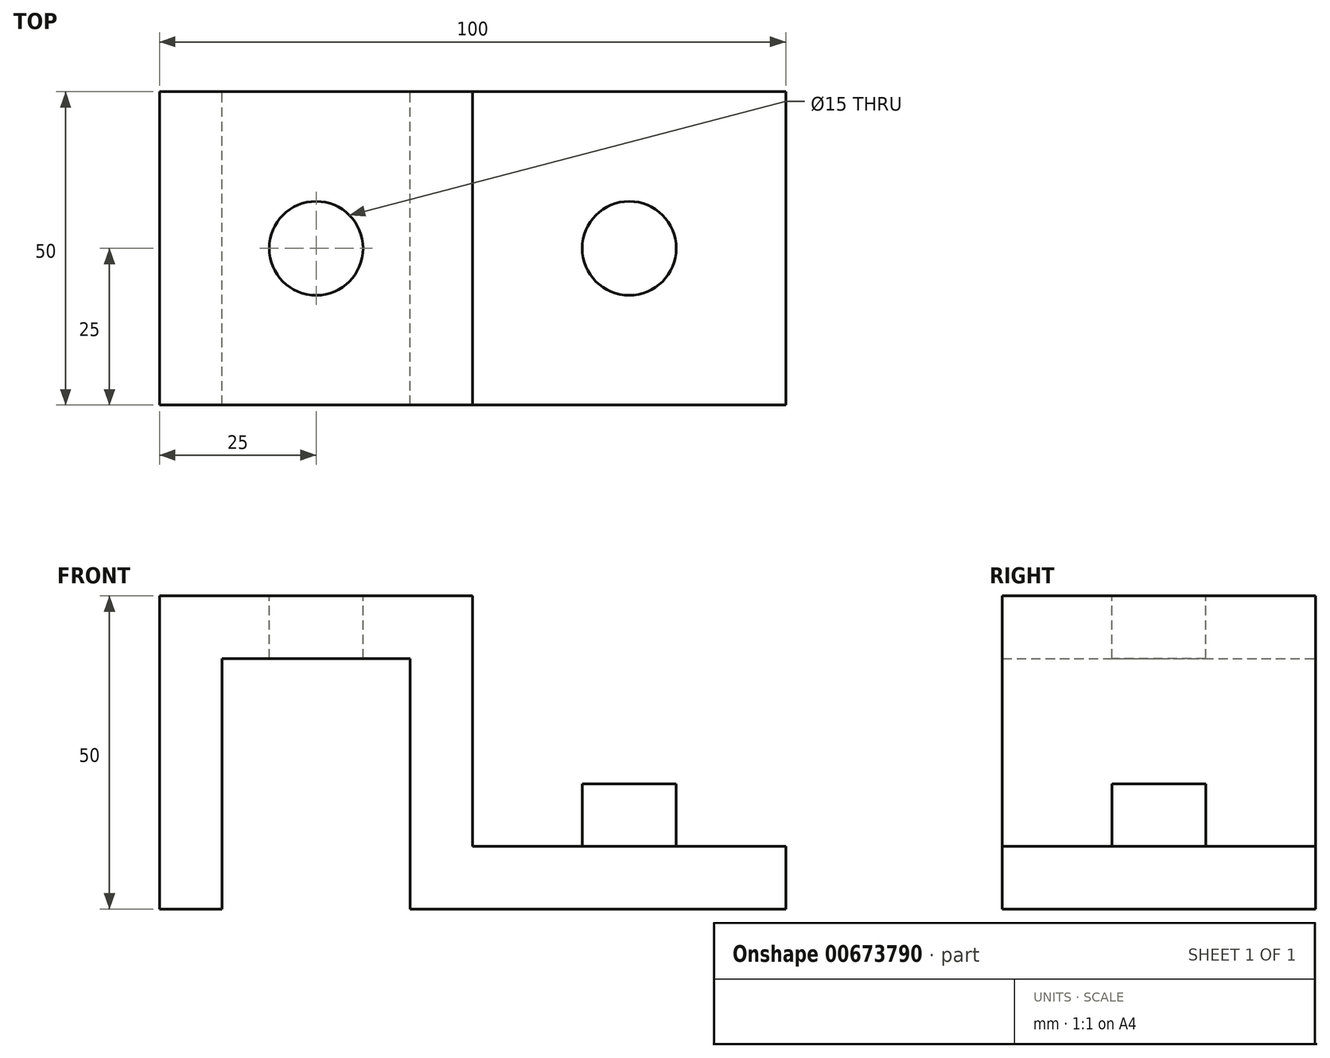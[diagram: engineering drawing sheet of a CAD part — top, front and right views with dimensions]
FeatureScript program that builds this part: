
annotation { "Feature Type Name" : "Feature", "Feature Type Description" : "" }
export const myFeature = defineFeature(function(context is Context, id is Id, definition is map)
    precondition{}
    {
        {
            var Q0;
            Q0=qCreatedBy(makeId("Front.planeOp"),FACE);
            var sketch = newSketch(context, id + "F0", { "sketchPlane" : qUnion([Q0])});
            skLineSegment(sketch, "E0", {"start": v(10, 0) * mm, "end": v(10, 40) * mm});
            skLineSegment(sketch, "E1", {"start": v(10, 40) * mm, "end": v(40, 40) * mm});
            skLineSegment(sketch, "E2", {"start": v(40, 40) * mm, "end": v(40, 0) * mm});
            skLineSegment(sketch, "E3", {"start": v(40, 0) * mm, "end": v(100, 0) * mm});
            skLineSegment(sketch, "E4.0", {"start": v(50, 10) * mm, "end": v(100, 10) * mm});
            skLineSegment(sketch, "E4.1", {"start": v(50, 50) * mm, "end": v(50, 10) * mm});
            skLineSegment(sketch, "E4.2", {"start": v(0, 50) * mm, "end": v(50, 50) * mm});
            skLineSegment(sketch, "E4.3", {"start": v(0, 0) * mm, "end": v(0, 50) * mm});
            skLineSegment(sketch, "E5", {"start": v(0, 0) * mm, "end": v(10, 0) * mm});
            skLineSegment(sketch, "E6", {"start": v(100, 10) * mm, "end": v(100, 0) * mm});
            skSolve(sketch);
        }
        {
            var Q0;
            Q0 = qSketchRegion(id + "F0", true);
            extrude(context, id + "F1", {"entities" : qUnion([Q0]), "endBound" : BoundingType.SYMMETRIC, "depth" : 50 * mm, "offsetDistance" : 25 * mm});
        }
        {
            var Q0;
            Q0=makeQuery(id+"F1.opExtrude","SWEPT_FACE",FACE,{"disambiguationData":[OSD([sQuery(id+"F0.wireOp",EDGE,"E4.2")])]});
            var sketch = newSketch(context, id + "F2", { "sketchPlane" : qUnion([Q0])});
            skCircle(sketch, "E7", {"center": v(25, 0) * mm, "radius": 7.5 * mm});
            skSolve(sketch);
        }
        {
            var Q0;
            Q0 = qSketchRegion(id + "F2", true);
            extrude(context, id + "F3", {"entities" : qUnion([Q0]), "operationType" : NewBodyOperationType.REMOVE, "oppositeDirection" : true, "depth" : 25 * mm, "offsetDistance" : 25 * mm});
        }
        {
            var Q0;
            Q0=makeQuery(id+"F1.opExtrude","SWEPT_FACE",FACE,{"disambiguationData":[OSD([sQuery(id+"F0.wireOp",EDGE,"E4.0")])]});
            var sketch = newSketch(context, id + "F4", { "sketchPlane" : qUnion([Q0])});
            skCircle(sketch, "E8", {"center": v(75, 0) * mm, "radius": 7.5 * mm});
            skSolve(sketch);
        }
        {
            var Q0;
            Q0 = qSketchRegion(id + "F4", true);
            var Q1;
            Q1=makeQuery(id+"F1.opExtrude","SWEPT_FACE",FACE,{"disambiguationData":[OSD([sQuery(id+"F0.wireOp",EDGE,"E3")])]});
            extrude(context, id + "F5", {"entities" : qUnion([Q0]), "operationType" : NewBodyOperationType.ADD, "depth" : 10 * mm, "endBoundEntityFace" : qUnion([Q1]), "offsetDistance" : 25 * mm});
        }
    });
